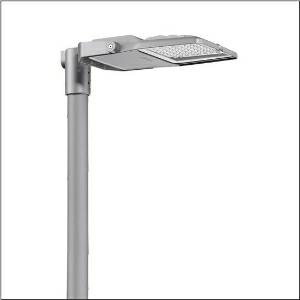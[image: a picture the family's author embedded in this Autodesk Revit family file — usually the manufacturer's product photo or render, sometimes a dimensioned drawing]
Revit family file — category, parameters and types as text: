
# Revit family: floodlight_fl_21_mini___pl61_5xa7776d2c3a_4c8f
name_source: partatom
category: Lighting Fixtures
units: mm (PartAtom-declared; Revit-internal decimal feet)

## family parameters
Cut with Voids When Loaded = No
Host = Face
Light Source = No
Part Type = Normal
Room Calculation Point = No
Round Connector Dimension = Use Diameter
Shared = No

## types (1)
- --- (1 x LED, 17510 lm, 142.9 W, 3000K)
    Apparent Load = 143 VA
    CIE Flux Codes = 33 65 98 100 100
    Color Rendering = 70
    Color Temperature = 3000K
    Default Elevation = 1800 mm
    Description = Floodlight FL 21 mini, floodlight, primary light control with lens, of PMMA, primary optical cover: protective disc, of toughened safety glass, transparent, light distribution: PL61, light emission: direct distribution, installation type: surface-mounted, LED, High Power LED, rated luminous flux: 17.510lm, luminous efficacy: 123lm/W, light colour: 730, colour temperature: 3000K, control gear: Smart Interface (Zhaga), control: flexible luminous flux parameterisation, time-dependent luminous flux control, constant luminous flux control, overheat protection, pre-setting: logarithmic dimming characteristic, with terminal, 6-pole, mains connection: 220..240V, AC, 50/60Hz, start of lifetime: 143W, end of service life: 151W, reduction: 63W, luminaire housing, of diecast aluminium, powder-coated, Siteco® metallic grey (DB 702S), corrosivity category C5 mid according to DIN EN ISO 12944, suitable for swimming pools, chlorine-resistant, sealing non-destructively replaceable, please order mast flange separately, mast bracket, of steel, galvanised, powder-coated, Siteco® metallic grey (DB 702S), Smart Interface below and above, protection rating (complete): IP66, insulation class (complete): insulation class II (safety insulation), certification: CE, ENEC, VDE, protection symbol: D, impact resistance: IK08, permissible operating ambient temperature: -40..+40°C, permissible operating ambient temperature for outdoor applications: -40..+50°C, standard: DIN EN 12944, LABS conformity tested according to VDMA 24364:2018-05, packaging unit: 1 piece

Light Distribution: PL61
    Height = 70 mm
    Lamp = 1 x LED
    Lamp Light Flux = 17510 lm
    Lamp Power = 142.9 W
    Lamp count = 1
    Length = 485 mm
    Luminous efficacy = 123 lm/W
    Manufacturer = Siteco
    ModVariant = No
    Model = 5XA7776D2C3A
    Number of Poles = 1
    OnlyDefault = Yes
    Power Factor = 1
    Product Name = Floodlight FL 21 mini | PL61
    Product group = floodlight | pylon annexe
    ProductGroupID = 6201
    Protection Class = Protection class II
    Protection Degree = IP 66
    RLX_Detail_Level = 1
    RLX_Emergency_Light_Flux = 0 lm
    RLX_Emergency_Type = 0
    RLX_Emergency_Type_DB = No
    RlxData = <blob elided: 101413 chars, md5=c080ae12>
    Socket = socket
    Standby Power = 0 W
    System Light Flux = 17510 lm
    System Power = 143 W
    Type Comments = factory setting: luminous flux: 100 % | dim-lin: 254 | 730 mA
    Type Image = l_1007125.jpg
    URL = http://relux.com
    VarID = @adj_193319
    Voltage = 0 V
    Weight = 0.00 kg
    Width = 337 mm

## geometry (parser evidence)
native form markers: Blend x4, Sweep x12
no freeform markers — native parametric forms only
